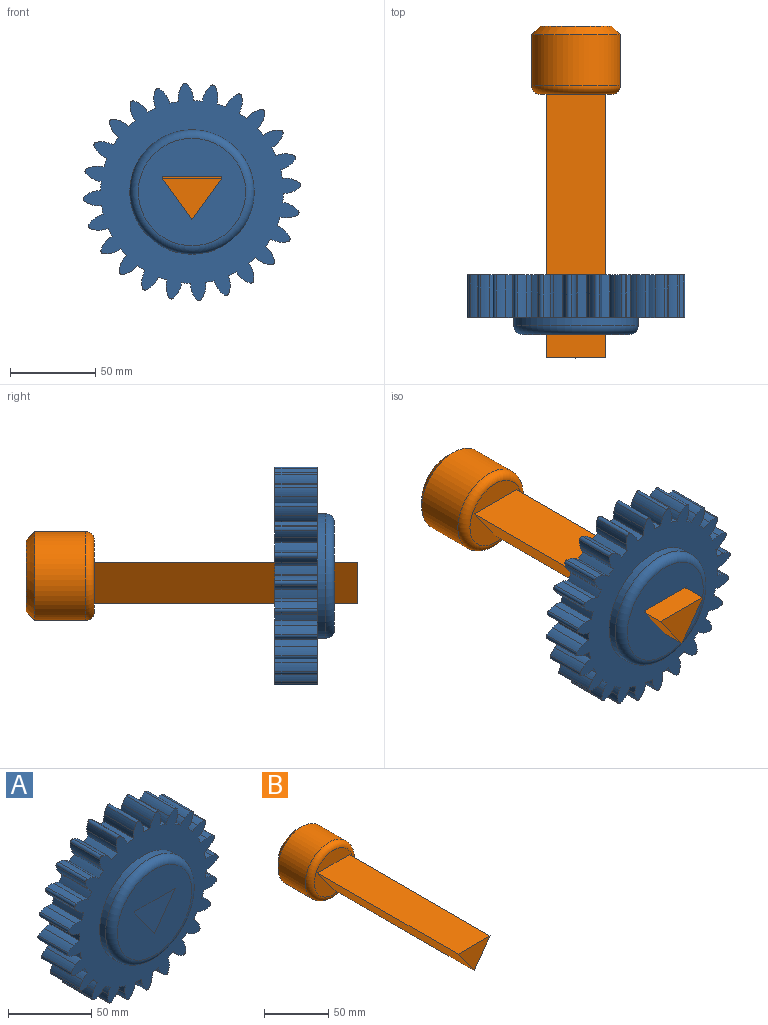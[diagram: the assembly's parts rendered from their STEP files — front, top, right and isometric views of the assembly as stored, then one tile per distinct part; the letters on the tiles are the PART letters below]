
ASSEMBLY  parts=2 mates=1
PART A: 152 faces, bbox 127.9x35x127.9 mm
  f0: cylinder r=53.72mm len=25mm, axis (0,1,0), area 131.8mm2, adj f23,f29,f30,f95
  f1: cylinder r=53.72mm len=25mm, axis (0,1,0), area 131.8mm2, adj f29,f30,f90,f94
  f2: cylinder r=53.72mm len=25mm, axis (0,1,0), area 131.8mm2, adj f29,f30,f85,f89
  f3: cylinder r=53.72mm len=25mm, axis (0,1,0), area 131.8mm2, adj f29,f30,f80,f84
  f4: cylinder r=53.72mm len=25mm, axis (0,1,0), area 131.8mm2, adj f29,f30,f75,f79
  f5: cylinder r=53.72mm len=25mm, axis (0,1,0), area 131.8mm2, adj f29,f30,f70,f74
  f6: cylinder r=53.72mm len=25mm, axis (0,1,0), area 131.8mm2, adj f29,f30,f65,f69
  f7: cylinder r=53.72mm len=25mm, axis (0,1,0), area 131.8mm2, adj f29,f30,f60,f64
  f8: cylinder r=53.72mm len=25mm, axis (0,1,0), area 131.8mm2, adj f29,f30,f55,f59
  f9: cylinder r=53.72mm len=25mm, axis (0,1,0), area 131.8mm2, adj f29,f30,f50,f54
  f10: cylinder r=53.72mm len=25mm, axis (0,1,0), area 131.8mm2, adj f29,f30,f45,f49
  f11: cylinder r=53.72mm len=25mm, axis (0,1,0), area 131.8mm2, adj f29,f30,f40,f44
  f12: cylinder r=53.72mm len=25mm, axis (0,1,0), area 131.8mm2, adj f29,f30,f39,f147
  f13: cylinder r=53.72mm len=25mm, axis (0,1,0), area 131.8mm2, adj f29,f30,f145,f146
  f14: cylinder r=53.72mm len=25mm, axis (0,1,0), area 131.8mm2, adj f29,f30,f140,f144
  f15: cylinder r=53.72mm len=25mm, axis (0,1,0), area 131.8mm2, adj f29,f30,f135,f139
  f16: cylinder r=53.72mm len=25mm, axis (0,1,0), area 131.8mm2, adj f29,f30,f130,f134
  f17: cylinder r=53.72mm len=25mm, axis (0,1,0), area 131.8mm2, adj f29,f30,f125,f129
  f18: cylinder r=53.72mm len=25mm, axis (0,1,0), area 131.8mm2, adj f29,f30,f120,f124
  f19: cylinder r=53.72mm len=25mm, axis (0,1,0), area 131.8mm2, adj f29,f30,f115,f119
  f20: cylinder r=53.72mm len=25mm, axis (0,1,0), area 131.8mm2, adj f29,f30,f110,f114
  f21: cylinder r=53.72mm len=25mm, axis (0,1,0), area 131.8mm2, adj f29,f30,f105,f109
  f22: cylinder r=53.72mm len=25mm, axis (0,1,0), area 131.8mm2, adj f29,f30,f99,f104
  f23: cylinder r=14.51mm len=25mm, axis (0,1,0), area 126.6mm2, adj f0,f28,f29,f30
  f24: cylinder r=53.72mm len=25mm, axis (0,1,0), area 131.8mm2, adj f25,f29,f30,f100
  f25: cylinder r=14.51mm len=25mm, axis (0,1,0), area 126.6mm2, adj f24,f26,f29,f30
  f26: cylinder r=14.44mm len=25mm, axis (0,1,0), area 139.7mm2, adj f25,f27,f29,f30
  f27: cylinder r=1.73mm len=25mm, axis (0,1,0), area 73.5mm2, adj f26,f28,f29,f30
  f28: cylinder r=14.44mm len=25mm, axis (0,1,0), area 139.7mm2, adj f23,f27,f29,f30
  f29: plane 127.88x127.88mm, normal (0,-1,0), area 6549.8mm2, adj f0,f1,f2,f3,f4,f5,f6,f7
  f30: plane 127.88x127.88mm, normal (0,1,0), area 10321.4mm2, adj f0,f1,f2,f3,f4,f5,f6,f7
  f31: plane 35x35mm, normal (0,0,-1), area 1225mm2, adj f30,f32,f33,f35
  f32: plane 35x24.37mm, normal (-0.81,0,0.58), area 1050mm2, adj f30,f31,f33,f35
  f33: plane 63.11x63.11mm, normal (0,-1,0), area 2701.7mm2, adj f31,f32,f35,f151
  f34: cylinder r=36.56mm len=73.11mm, axis (0,1,0), area 1148.4mm2, adj f29,f151
  f35: plane 35x24.37mm, normal (0.81,0,0.58), area 1050mm2, adj f30,f31,f32,f33
  f36: cylinder r=14.44mm len=25mm, axis (0,1,0), area 139.7mm2, adj f29,f30,f37,f40
  f37: cylinder r=1.73mm len=25mm, axis (0,1,0), area 73.5mm2, adj f29,f30,f36,f38
  f38: cylinder r=14.44mm len=25mm, axis (0,1,0), area 139.7mm2, adj f29,f30,f37,f39
  f39: cylinder r=14.51mm len=25mm, axis (0,1,0), area 126.6mm2, adj f12,f29,f30,f38
  f40: cylinder r=14.51mm len=25mm, axis (0,1,0), area 126.6mm2, adj f11,f29,f30,f36
  f41: cylinder r=14.44mm len=25mm, axis (0,1,0), area 139.7mm2, adj f29,f30,f42,f45
  f42: cylinder r=1.73mm len=25mm, axis (0,1,0), area 73.5mm2, adj f29,f30,f41,f43
  f43: cylinder r=14.44mm len=25mm, axis (0,1,0), area 139.7mm2, adj f29,f30,f42,f44
  f44: cylinder r=14.51mm len=25mm, axis (0,1,0), area 126.6mm2, adj f11,f29,f30,f43
  f45: cylinder r=14.51mm len=25mm, axis (0,1,0), area 126.6mm2, adj f10,f29,f30,f41
  f46: cylinder r=14.44mm len=25mm, axis (0,1,0), area 139.7mm2, adj f29,f30,f47,f50
  f47: cylinder r=1.73mm len=25mm, axis (0,1,0), area 73.5mm2, adj f29,f30,f46,f48
  f48: cylinder r=14.44mm len=25mm, axis (0,1,0), area 139.7mm2, adj f29,f30,f47,f49
  f49: cylinder r=14.51mm len=25mm, axis (0,1,0), area 126.6mm2, adj f10,f29,f30,f48
  f50: cylinder r=14.51mm len=25mm, axis (0,1,0), area 126.6mm2, adj f9,f29,f30,f46
  f51: cylinder r=14.44mm len=25mm, axis (0,1,0), area 139.7mm2, adj f29,f30,f52,f55
  f52: cylinder r=1.73mm len=25mm, axis (0,1,0), area 73.5mm2, adj f29,f30,f51,f53
  f53: cylinder r=14.44mm len=25mm, axis (0,1,0), area 139.7mm2, adj f29,f30,f52,f54
  f54: cylinder r=14.51mm len=25mm, axis (0,1,0), area 126.6mm2, adj f9,f29,f30,f53
  f55: cylinder r=14.51mm len=25mm, axis (0,1,0), area 126.6mm2, adj f8,f29,f30,f51
  f56: cylinder r=14.44mm len=25mm, axis (0,1,0), area 139.7mm2, adj f29,f30,f57,f60
  f57: cylinder r=1.73mm len=25mm, axis (0,1,0), area 73.5mm2, adj f29,f30,f56,f58
  f58: cylinder r=14.44mm len=25mm, axis (0,1,0), area 139.7mm2, adj f29,f30,f57,f59
  f59: cylinder r=14.51mm len=25mm, axis (0,1,0), area 126.6mm2, adj f8,f29,f30,f58
  f60: cylinder r=14.51mm len=25mm, axis (0,1,0), area 126.6mm2, adj f7,f29,f30,f56
  f61: cylinder r=14.44mm len=25mm, axis (0,1,0), area 139.7mm2, adj f29,f30,f62,f65
  f62: cylinder r=1.73mm len=25mm, axis (0,1,0), area 73.5mm2, adj f29,f30,f61,f63
  f63: cylinder r=14.44mm len=25mm, axis (0,1,0), area 139.7mm2, adj f29,f30,f62,f64
  f64: cylinder r=14.51mm len=25mm, axis (0,1,0), area 126.6mm2, adj f7,f29,f30,f63
  f65: cylinder r=14.51mm len=25mm, axis (0,1,0), area 126.6mm2, adj f6,f29,f30,f61
  f66: cylinder r=14.44mm len=25mm, axis (0,1,0), area 139.7mm2, adj f29,f30,f67,f70
  f67: cylinder r=1.73mm len=25mm, axis (0,1,0), area 73.5mm2, adj f29,f30,f66,f68
  f68: cylinder r=14.44mm len=25mm, axis (0,1,0), area 139.7mm2, adj f29,f30,f67,f69
  f69: cylinder r=14.51mm len=25mm, axis (0,1,0), area 126.6mm2, adj f6,f29,f30,f68
  f70: cylinder r=14.51mm len=25mm, axis (0,1,0), area 126.6mm2, adj f5,f29,f30,f66
  f71: cylinder r=14.44mm len=25mm, axis (0,1,0), area 139.7mm2, adj f29,f30,f72,f75
  f72: cylinder r=1.73mm len=25mm, axis (0,1,0), area 73.5mm2, adj f29,f30,f71,f73
  f73: cylinder r=14.44mm len=25mm, axis (0,1,0), area 139.7mm2, adj f29,f30,f72,f74
  f74: cylinder r=14.51mm len=25mm, axis (0,1,0), area 126.6mm2, adj f5,f29,f30,f73
  f75: cylinder r=14.51mm len=25mm, axis (0,1,0), area 126.6mm2, adj f4,f29,f30,f71
  f76: cylinder r=14.44mm len=25mm, axis (0,1,0), area 139.7mm2, adj f29,f30,f77,f80
  f77: cylinder r=1.73mm len=25mm, axis (0,1,0), area 73.5mm2, adj f29,f30,f76,f78
  f78: cylinder r=14.44mm len=25mm, axis (0,1,0), area 139.7mm2, adj f29,f30,f77,f79
  f79: cylinder r=14.51mm len=25mm, axis (0,1,0), area 126.6mm2, adj f4,f29,f30,f78
  f80: cylinder r=14.51mm len=25mm, axis (0,1,0), area 126.6mm2, adj f3,f29,f30,f76
  f81: cylinder r=14.44mm len=25mm, axis (0,1,0), area 139.7mm2, adj f29,f30,f82,f85
  f82: cylinder r=1.73mm len=25mm, axis (0,1,0), area 73.5mm2, adj f29,f30,f81,f83
  f83: cylinder r=14.44mm len=25mm, axis (0,1,0), area 139.7mm2, adj f29,f30,f82,f84
  f84: cylinder r=14.51mm len=25mm, axis (0,1,0), area 126.6mm2, adj f3,f29,f30,f83
  f85: cylinder r=14.51mm len=25mm, axis (0,1,0), area 126.6mm2, adj f2,f29,f30,f81
  f86: cylinder r=14.44mm len=25mm, axis (0,1,0), area 139.7mm2, adj f29,f30,f87,f90
  f87: cylinder r=1.73mm len=25mm, axis (0,1,0), area 73.5mm2, adj f29,f30,f86,f88
  f88: cylinder r=14.44mm len=25mm, axis (0,1,0), area 139.7mm2, adj f29,f30,f87,f89
  f89: cylinder r=14.51mm len=25mm, axis (0,1,0), area 126.6mm2, adj f2,f29,f30,f88
  f90: cylinder r=14.51mm len=25mm, axis (0,1,0), area 126.6mm2, adj f1,f29,f30,f86
  f91: cylinder r=14.44mm len=25mm, axis (0,1,0), area 139.7mm2, adj f29,f30,f92,f95
  f92: cylinder r=1.73mm len=25mm, axis (0,1,0), area 73.5mm2, adj f29,f30,f91,f93
  f93: cylinder r=14.44mm len=25mm, axis (0,1,0), area 139.7mm2, adj f29,f30,f92,f94
  f94: cylinder r=14.51mm len=25mm, axis (0,1,0), area 126.6mm2, adj f1,f29,f30,f93
  f95: cylinder r=14.51mm len=25mm, axis (0,1,0), area 126.6mm2, adj f0,f29,f30,f91
  f96: cylinder r=14.44mm len=25mm, axis (0,1,0), area 139.7mm2, adj f29,f30,f97,f99
  f97: cylinder r=1.73mm len=25mm, axis (0,1,0), area 73.5mm2, adj f29,f30,f96,f98
  f98: cylinder r=14.44mm len=25mm, axis (0,1,0), area 139.7mm2, adj f29,f30,f97,f100
  f99: cylinder r=14.51mm len=25mm, axis (0,1,0), area 126.6mm2, adj f22,f29,f30,f96
  f100: cylinder r=14.51mm len=25mm, axis (0,1,0), area 126.6mm2, adj f24,f29,f30,f98
  f101: cylinder r=14.44mm len=25mm, axis (0,1,0), area 139.7mm2, adj f29,f30,f102,f105
  f102: cylinder r=1.73mm len=25mm, axis (0,1,0), area 73.5mm2, adj f29,f30,f101,f103
  f103: cylinder r=14.44mm len=25mm, axis (0,1,0), area 139.7mm2, adj f29,f30,f102,f104
  f104: cylinder r=14.51mm len=25mm, axis (0,1,0), area 126.6mm2, adj f22,f29,f30,f103
  f105: cylinder r=14.51mm len=25mm, axis (0,1,0), area 126.6mm2, adj f21,f29,f30,f101
  f106: cylinder r=14.44mm len=25mm, axis (0,1,0), area 139.7mm2, adj f29,f30,f107,f110
  f107: cylinder r=1.73mm len=25mm, axis (0,1,0), area 73.5mm2, adj f29,f30,f106,f108
  f108: cylinder r=14.44mm len=25mm, axis (0,1,0), area 139.7mm2, adj f29,f30,f107,f109
  f109: cylinder r=14.51mm len=25mm, axis (0,1,0), area 126.6mm2, adj f21,f29,f30,f108
  f110: cylinder r=14.51mm len=25mm, axis (0,1,0), area 126.6mm2, adj f20,f29,f30,f106
  f111: cylinder r=14.44mm len=25mm, axis (0,1,0), area 139.7mm2, adj f29,f30,f112,f115
  f112: cylinder r=1.73mm len=25mm, axis (0,1,0), area 73.5mm2, adj f29,f30,f111,f113
  f113: cylinder r=14.44mm len=25mm, axis (0,1,0), area 139.7mm2, adj f29,f30,f112,f114
  f114: cylinder r=14.51mm len=25mm, axis (0,1,0), area 126.6mm2, adj f20,f29,f30,f113
  f115: cylinder r=14.51mm len=25mm, axis (0,1,0), area 126.6mm2, adj f19,f29,f30,f111
  f116: cylinder r=14.44mm len=25mm, axis (0,1,0), area 139.7mm2, adj f29,f30,f117,f120
  f117: cylinder r=1.73mm len=25mm, axis (0,1,0), area 73.5mm2, adj f29,f30,f116,f118
  f118: cylinder r=14.44mm len=25mm, axis (0,1,0), area 139.7mm2, adj f29,f30,f117,f119
  f119: cylinder r=14.51mm len=25mm, axis (0,1,0), area 126.6mm2, adj f19,f29,f30,f118
  f120: cylinder r=14.51mm len=25mm, axis (0,1,0), area 126.6mm2, adj f18,f29,f30,f116
  f121: cylinder r=14.44mm len=25mm, axis (0,1,0), area 139.7mm2, adj f29,f30,f122,f125
  f122: cylinder r=1.73mm len=25mm, axis (0,1,0), area 73.5mm2, adj f29,f30,f121,f123
  f123: cylinder r=14.44mm len=25mm, axis (0,1,0), area 139.7mm2, adj f29,f30,f122,f124
  f124: cylinder r=14.51mm len=25mm, axis (0,1,0), area 126.6mm2, adj f18,f29,f30,f123
  f125: cylinder r=14.51mm len=25mm, axis (0,1,0), area 126.6mm2, adj f17,f29,f30,f121
  f126: cylinder r=14.44mm len=25mm, axis (0,1,0), area 139.7mm2, adj f29,f30,f127,f130
  f127: cylinder r=1.73mm len=25mm, axis (0,1,0), area 73.5mm2, adj f29,f30,f126,f128
  f128: cylinder r=14.44mm len=25mm, axis (0,1,0), area 139.7mm2, adj f29,f30,f127,f129
  f129: cylinder r=14.51mm len=25mm, axis (0,1,0), area 126.6mm2, adj f17,f29,f30,f128
  f130: cylinder r=14.51mm len=25mm, axis (0,1,0), area 126.6mm2, adj f16,f29,f30,f126
  f131: cylinder r=14.44mm len=25mm, axis (0,1,0), area 139.7mm2, adj f29,f30,f132,f135
  f132: cylinder r=1.73mm len=25mm, axis (0,1,0), area 73.5mm2, adj f29,f30,f131,f133
  f133: cylinder r=14.44mm len=25mm, axis (0,1,0), area 139.7mm2, adj f29,f30,f132,f134
  f134: cylinder r=14.51mm len=25mm, axis (0,1,0), area 126.6mm2, adj f16,f29,f30,f133
  f135: cylinder r=14.51mm len=25mm, axis (0,1,0), area 126.6mm2, adj f15,f29,f30,f131
  f136: cylinder r=14.44mm len=25mm, axis (0,1,0), area 139.7mm2, adj f29,f30,f137,f140
  f137: cylinder r=1.73mm len=25mm, axis (0,1,0), area 73.5mm2, adj f29,f30,f136,f138
  f138: cylinder r=14.44mm len=25mm, axis (0,1,0), area 139.7mm2, adj f29,f30,f137,f139
  f139: cylinder r=14.51mm len=25mm, axis (0,1,0), area 126.6mm2, adj f15,f29,f30,f138
  f140: cylinder r=14.51mm len=25mm, axis (0,1,0), area 126.6mm2, adj f14,f29,f30,f136
  f141: cylinder r=14.44mm len=25mm, axis (0,1,0), area 139.7mm2, adj f29,f30,f142,f145
  f142: cylinder r=1.73mm len=25mm, axis (0,1,0), area 73.5mm2, adj f29,f30,f141,f143
  f143: cylinder r=14.44mm len=25mm, axis (0,1,0), area 139.7mm2, adj f29,f30,f142,f144
  f144: cylinder r=14.51mm len=25mm, axis (0,1,0), area 126.6mm2, adj f14,f29,f30,f143
  f145: cylinder r=14.51mm len=25mm, axis (0,1,0), area 126.6mm2, adj f13,f29,f30,f141
  f146: cylinder r=14.51mm len=25mm, axis (0,1,0), area 126.6mm2, adj f13,f29,f30,f150
  f147: cylinder r=14.51mm len=25mm, axis (0,1,0), area 126.6mm2, adj f12,f29,f30,f148
  f148: cylinder r=14.44mm len=25mm, axis (0,1,0), area 139.7mm2, adj f29,f30,f147,f149
  f149: cylinder r=1.73mm len=25mm, axis (0,1,0), area 73.5mm2, adj f29,f30,f148,f150
  f150: cylinder r=14.44mm len=25mm, axis (0,1,0), area 139.7mm2, adj f29,f30,f146,f149
  f151: torus R=31.56mm, axis (0,-1,0), area 1714.3mm2, adj f33,f34
PART B: 9 faces, bbox 56.5x195x56.5 mm
  f0: plane 155x35mm, normal (0,0,1), area 5425mm2, adj f1,f2,f3,f6
  f1: plane 155x24.37mm, normal (-0.81,0,-0.58), area 4650mm2, adj f0,f2,f3,f6
  f2: plane 155x24.37mm, normal (0.81,0,-0.58), area 4650mm2, adj f0,f1,f3,f6
  f3: plane 35x24.37mm, normal (0,-1,0), area 426.4mm2, adj f0,f1,f2
  f4: cylinder r=26.11mm len=52.22mm, axis (0,-1,0), area 4921.5mm2, adj f7,f8
  f5: plane 42.22x42.22mm, normal (0,1,0), area 1399.9mm2, adj f7
  f6: plane 42.22x42.22mm, normal (0,-1,0), area 973.5mm2, adj f0,f1,f2,f8
  f7: cone r=26.11mm half-angle=45deg, axis (0,-1,0), area 1048.9mm2, adj f4,f5
  f8: torus R=21.11mm, axis (0,-1,0), area 1198.8mm2, adj f4,f6
PLACE A rot(axis=(0,1,0),0deg) t=(172.02,218.12,-111.34)mm
PLACE B rot(axis=(0,1,0),0deg) t=(172.02,324.34,-111.34)mm
MATE slider B.f4 <-> A.f34  axis (0,-1,0) through (172.02,169.34,-111.34)mm
